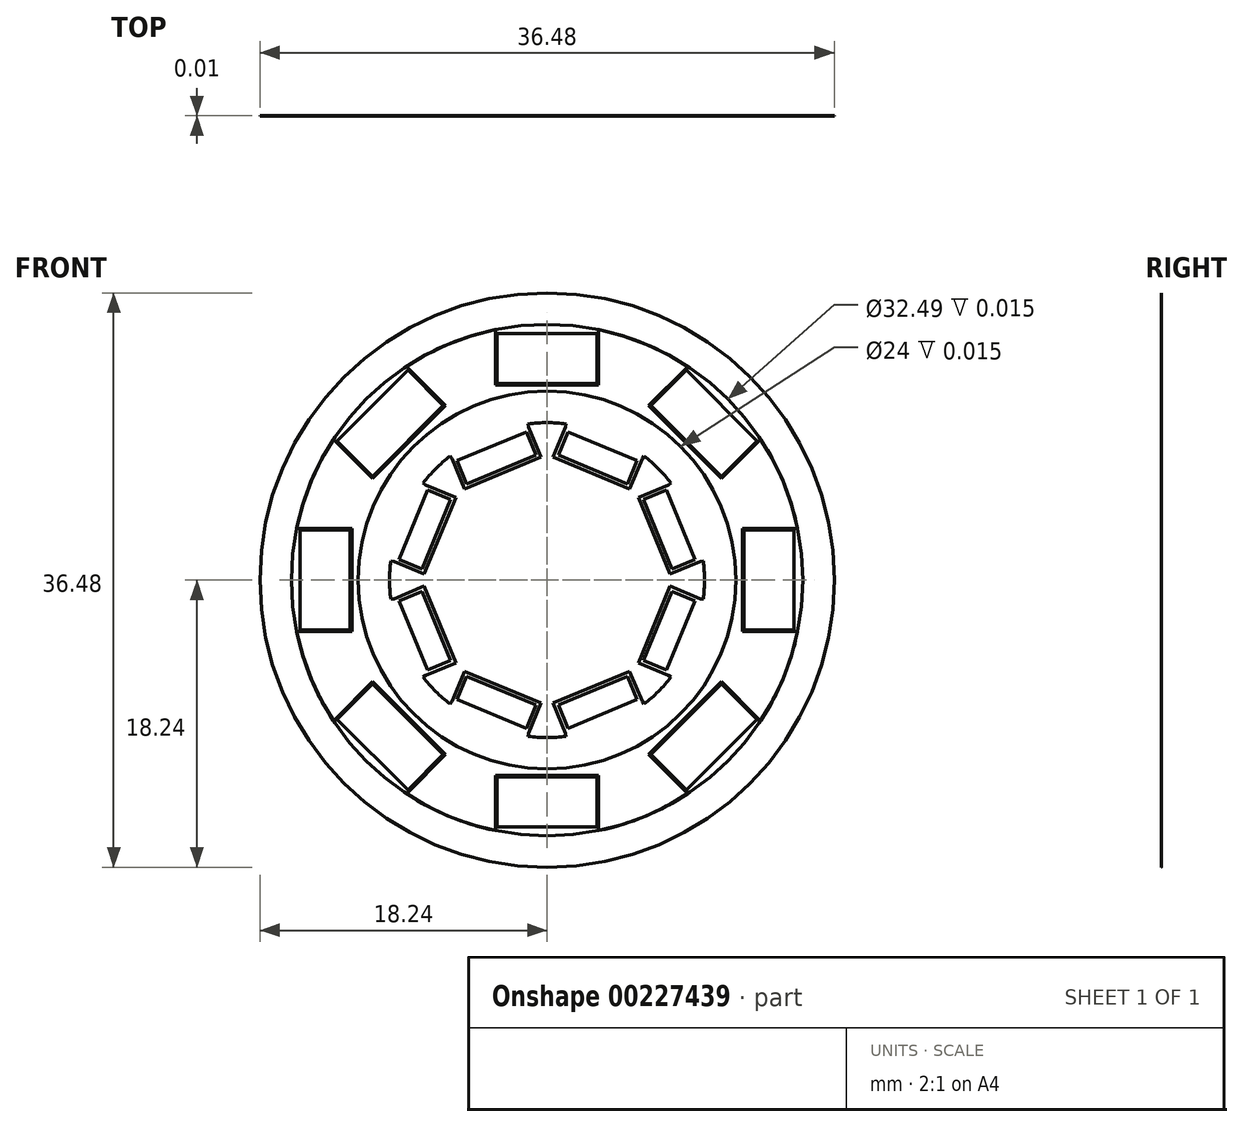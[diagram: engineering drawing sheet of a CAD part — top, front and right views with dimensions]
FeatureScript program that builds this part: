
annotation { "Feature Type Name" : "Feature", "Feature Type Description" : "" }
export const myFeature = defineFeature(function(context is Context, id is Id, definition is map)
    precondition{}
    {
        {
            var Q0;
            Q0=qCreatedBy(makeId("Front.planeOp"),FACE);
            var sketch = newSketch(context, id + "F0", { "sketchPlane" : qUnion([Q0])});
            skLineSegment(sketch, "E0.bottom", {"start": v(-3.17, 12.5) * mm, "end": v(3.17, 12.5) * mm});
            skLineSegment(sketch, "E0.top", {"start": v(-3.17, 15.68) * mm, "end": v(3.17, 15.68) * mm});
            skLineSegment(sketch, "E0.left", {"start": v(-3.18, 12.5) * mm, "end": v(-3.18, 15.68) * mm});
            skLineSegment(sketch, "E0.right", {"start": v(3.17, 12.5) * mm, "end": v(3.17, 15.68) * mm});
            skCircle(sketch, "E1", {"center": v(0, 0) * mm, "radius": 12.5 * mm, "construction": true});
            skCircle(sketch, "E2", {"center": v(0, 0) * mm, "radius": 9.5 * mm, "construction": true});
            skPoint(sketch, "E3.firstSnap0", {"position": v(-3.17, 14.09) * mm});
            skLineSegment(sketch, "E4", {"start": v(0, 0) * mm, "end": v(0, 38.25) * mm, "construction": true});
            skLineSegment(sketch, "E5.bottom", {"start": v(-2.38, 7.6) * mm, "end": v(2.38, 7.6) * mm});
            skLineSegment(sketch, "E5.top", {"start": v(-2.38, 9.2) * mm, "end": v(2.38, 9.2) * mm});
            skLineSegment(sketch, "E5.left", {"start": v(-2.38, 7.6) * mm, "end": v(-2.38, 9.2) * mm});
            skLineSegment(sketch, "E5.right", {"start": v(2.38, 7.6) * mm, "end": v(2.38, 9.2) * mm});
            skCircle(sketch, "E6", {"center": v(0, 0) * mm, "radius": 16 * mm, "construction": true});
            skCircle(sketch, "E7", {"center": v(0, 0) * mm, "radius": 18.24 * mm});
            skCircle(sketch, "E8", {"center": v(0, 0) * mm, "radius": 7.6 * mm, "construction": true});
            skCircle(sketch, "E9", {"center": v(0, 0) * mm, "radius": 5.36 * mm});
            skCircle(sketch, "E10", {"center": v(0, 0) * mm, "radius": 16.24 * mm});
            skCircle(sketch, "E11", {"center": v(0, 0) * mm, "radius": 7.36 * mm});
            skSolve(sketch);
        }
        {
            var Q0;
            Q0=makeQuery(id+"F0.imprint","IMPRINT",FACE,{"disambiguationData":[TD([[makeQuery(id+"F0.imprint","IMPRINT",EDGE,{"derivedFrom":sQuery(id+"F0.wireOp",EDGE,"E7")}),1.0]])]});
            var Q1;
            Q1=makeQuery(id+"F0.imprint","IMPRINT",FACE,{"disambiguationData":[TD([[makeQuery(id+"F0.imprint","IMPRINT",EDGE,{"derivedFrom":sQuery(id+"F0.wireOp",EDGE,"E0.bottom")}),1.0]])]});
            var Q2;
            Q2=makeQuery(id+"F0.imprint","IMPRINT",FACE,{"disambiguationData":[TD([[makeQuery(id+"F0.imprint","IMPRINT",EDGE,{"derivedFrom":sQuery(id+"F0.wireOp",EDGE,"E5.bottom")}),1.0]])]});
            var Q3;
            Q3=makeQuery(id+"F0.imprint","IMPRINT",FACE,{"disambiguationData":[TD([[makeQuery(id+"F0.imprint","IMPRINT",EDGE,{"derivedFrom":sQuery(id+"F0.wireOp",EDGE,"E9")}),-1.0]])]});
            extrude(context, id + "F1", {"entities" : qUnion([Q0, Q1, Q2, Q3]), "depth" : 3 / 203.2 * mm});
        }
        {
            var Q0;
            Q0=qCreatedBy(makeId("Right.planeOp"),FACE);
            var sketch = newSketch(context, id + "F2", { "sketchPlane" : qUnion([Q0])});
            skLineSegment(sketch, "E12", {"start": v(0, 0) * mm, "end": v(120.85, 0) * mm});
            skSolve(sketch);
        }
        {
            var Q0;
            Q0=makeQuery(id+"F1.opExtrude","SWEPT_BODY",BODY,{"disambiguationData":[OSD([sQuery(id+"F0.wireOp",EDGE,"E5.bottom"),sQuery(id+"F0.wireOp",EDGE,"E5.top"),sQuery(id+"F0.wireOp",EDGE,"E5.left"),sQuery(id+"F0.wireOp",EDGE,"E5.right")])]});
            var Q1;
            Q1=makeQuery(id+"F1.opExtrude","SWEPT_BODY",BODY,{"disambiguationData":[OSD([sQuery(id+"F0.wireOp",EDGE,"E0.bottom"),sQuery(id+"F0.wireOp",EDGE,"E0.top"),sQuery(id+"F0.wireOp",EDGE,"E0.left"),sQuery(id+"F0.wireOp",EDGE,"E0.right")])]});
            var Q2;
            Q2=sQuery(id+"F2.wireOp",EDGE,"E12");
            circularPattern(context, id + "F3", {"entities" : qUnion([Q0, Q1]), "axis" : qUnion([Q2]), "angle" : 360 * degree, "instanceCount" : 8, "equalSpace" : true});
        }
        {
            var Q0;
            Q0=qCreatedBy(makeId("Front.planeOp"),FACE);
            var sketch = newSketch(context, id + "F4", { "sketchPlane" : qUnion([Q0])});
            skCircle(sketch, "E13.0", {"center": v(0, 0) * mm, "radius": 7.36 * mm});
            skArc(sketch, "E14", {"start": v(-8.7, 4.91) * mm, "mid": v(-9.24, 3.83) * mm, "end": v(-9.63, 2.68) * mm});
            skLineSegment(sketch, "E15.1", {"start": v(2.63, 7.36) * mm, "end": v(2.63, 9.45) * mm});
            skLineSegment(sketch, "E15.2", {"start": v(-2.63, 7.36) * mm, "end": v(2.63, 7.36) * mm});
            skLineSegment(sketch, "E15.3", {"start": v(-2.63, 9.45) * mm, "end": v(-2.63, 7.36) * mm});
            skLineSegment(sketch, "E16", {"start": v(-2.63, 9.45) * mm, "end": v(-2.68, 9.63) * mm});
            skLineSegment(sketch, "E17", {"start": v(2.63, 9.45) * mm, "end": v(2.68, 9.63) * mm});
            skLineSegment(sketch, "E18.1.0", {"start": v(-3.34, 7.06) * mm, "end": v(-4.82, 8.54) * mm});
            skLineSegment(sketch, "E18.1.1", {"start": v(-8.54, 4.82) * mm, "end": v(-7.06, 3.34) * mm});
            skLineSegment(sketch, "E18.1.2", {"start": v(-7.06, 3.34) * mm, "end": v(-3.34, 7.06) * mm});
            skLineSegment(sketch, "E18.1.3", {"start": v(-4.82, 8.54) * mm, "end": v(-4.91, 8.7) * mm});
            skLineSegment(sketch, "E18.1.4", {"start": v(-8.54, 4.82) * mm, "end": v(-8.7, 4.91) * mm});
            skLineSegment(sketch, "E18.2.0", {"start": v(-7.36, 2.63) * mm, "end": v(-9.45, 2.63) * mm});
            skLineSegment(sketch, "E18.2.1", {"start": v(-9.45, -2.63) * mm, "end": v(-7.36, -2.63) * mm});
            skLineSegment(sketch, "E18.2.2", {"start": v(-7.36, -2.63) * mm, "end": v(-7.36, 2.63) * mm});
            skLineSegment(sketch, "E18.2.3", {"start": v(-9.45, 2.63) * mm, "end": v(-9.63, 2.68) * mm});
            skLineSegment(sketch, "E18.2.4", {"start": v(-9.45, -2.63) * mm, "end": v(-9.63, -2.68) * mm});
            skLineSegment(sketch, "E18.3.0", {"start": v(-7.06, -3.34) * mm, "end": v(-8.54, -4.82) * mm});
            skLineSegment(sketch, "E18.3.1", {"start": v(-4.82, -8.54) * mm, "end": v(-3.34, -7.06) * mm});
            skLineSegment(sketch, "E18.3.2", {"start": v(-3.34, -7.06) * mm, "end": v(-7.06, -3.34) * mm});
            skLineSegment(sketch, "E18.3.3", {"start": v(-8.54, -4.82) * mm, "end": v(-8.7, -4.91) * mm});
            skLineSegment(sketch, "E18.3.4", {"start": v(-4.82, -8.54) * mm, "end": v(-4.91, -8.7) * mm});
            skLineSegment(sketch, "E18.4.0", {"start": v(-2.63, -7.36) * mm, "end": v(-2.63, -9.45) * mm});
            skLineSegment(sketch, "E18.4.1", {"start": v(2.63, -9.45) * mm, "end": v(2.63, -7.36) * mm});
            skLineSegment(sketch, "E18.4.2", {"start": v(2.63, -7.36) * mm, "end": v(-2.63, -7.36) * mm});
            skLineSegment(sketch, "E18.4.3", {"start": v(-2.63, -9.45) * mm, "end": v(-2.68, -9.63) * mm});
            skLineSegment(sketch, "E18.4.4", {"start": v(2.63, -9.45) * mm, "end": v(2.68, -9.63) * mm});
            skLineSegment(sketch, "E18.5.0", {"start": v(3.34, -7.06) * mm, "end": v(4.82, -8.54) * mm});
            skLineSegment(sketch, "E18.5.1", {"start": v(8.54, -4.82) * mm, "end": v(7.06, -3.34) * mm});
            skLineSegment(sketch, "E18.5.2", {"start": v(7.06, -3.34) * mm, "end": v(3.34, -7.06) * mm});
            skLineSegment(sketch, "E18.5.3", {"start": v(4.82, -8.54) * mm, "end": v(4.91, -8.7) * mm});
            skLineSegment(sketch, "E18.5.4", {"start": v(8.54, -4.82) * mm, "end": v(8.7, -4.91) * mm});
            skLineSegment(sketch, "E18.6.0", {"start": v(7.36, -2.63) * mm, "end": v(9.45, -2.63) * mm});
            skLineSegment(sketch, "E18.6.1", {"start": v(9.45, 2.63) * mm, "end": v(7.36, 2.63) * mm});
            skLineSegment(sketch, "E18.6.2", {"start": v(7.36, 2.63) * mm, "end": v(7.36, -2.63) * mm});
            skLineSegment(sketch, "E18.6.3", {"start": v(9.45, -2.63) * mm, "end": v(9.63, -2.68) * mm});
            skLineSegment(sketch, "E18.6.4", {"start": v(9.45, 2.63) * mm, "end": v(9.63, 2.68) * mm});
            skLineSegment(sketch, "E18.7.0", {"start": v(7.06, 3.34) * mm, "end": v(8.54, 4.82) * mm});
            skLineSegment(sketch, "E18.7.1", {"start": v(4.82, 8.54) * mm, "end": v(3.34, 7.06) * mm});
            skLineSegment(sketch, "E18.7.2", {"start": v(3.34, 7.06) * mm, "end": v(7.06, 3.34) * mm});
            skLineSegment(sketch, "E18.7.3", {"start": v(8.54, 4.82) * mm, "end": v(8.7, 4.91) * mm});
            skLineSegment(sketch, "E18.7.4", {"start": v(4.82, 8.54) * mm, "end": v(4.91, 8.7) * mm});
            skArc(sketch, "E19.trimOffspring", {"start": v(-2.68, 9.63) * mm, "mid": v(-3.83, 9.24) * mm, "end": v(-4.91, 8.7) * mm});
            skArc(sketch, "E20.trimOffspring", {"start": v(4.91, 8.7) * mm, "mid": v(3.83, 9.24) * mm, "end": v(2.68, 9.63) * mm});
            skArc(sketch, "E21.trimOffspring", {"start": v(-9.63, -2.68) * mm, "mid": v(-9.24, -3.83) * mm, "end": v(-8.7, -4.91) * mm});
            skArc(sketch, "E22.trimOffspring", {"start": v(-4.91, -8.7) * mm, "mid": v(-3.83, -9.24) * mm, "end": v(-2.68, -9.63) * mm});
            skArc(sketch, "E23.trimOffspring", {"start": v(2.68, -9.63) * mm, "mid": v(3.83, -9.24) * mm, "end": v(4.91, -8.7) * mm});
            skArc(sketch, "E24.trimOffspring", {"start": v(8.7, -4.91) * mm, "mid": v(9.24, -3.83) * mm, "end": v(9.63, -2.68) * mm});
            skArc(sketch, "E25.trimOffspring", {"start": v(9.63, 2.68) * mm, "mid": v(9.24, 3.83) * mm, "end": v(8.7, 4.91) * mm});
            skSolve(sketch);
        }
        {
            var Q0;
            Q0 = qSketchRegion(id + "F4", true);
            extrude(context, id + "F5", {"entities" : qUnion([Q0]), "operationType" : NewBodyOperationType.ADD, "depth" : 3 / 203.2 * mm});
        }
        {
            var Q0;
            Q0=qCreatedBy(makeId("Front.planeOp"),FACE);
            var sketch = newSketch(context, id + "F6", { "sketchPlane" : qUnion([Q0])});
            skCircle(sketch, "E26", {"center": v(0, 0) * mm, "radius": 12 * mm});
            skArc(sketch, "E27.0", {"start": v(-13.58, 8.91) * mm, "mid": v(-15, 6.22) * mm, "end": v(-15.9, 3.3) * mm});
            skLineSegment(sketch, "E28.1", {"start": v(3.27, 12.4) * mm, "end": v(3.27, 15.78) * mm});
            skLineSegment(sketch, "E28.2", {"start": v(-3.28, 12.4) * mm, "end": v(3.27, 12.4) * mm});
            skLineSegment(sketch, "E28.3", {"start": v(-3.28, 15.78) * mm, "end": v(-3.28, 12.4) * mm});
            skLineSegment(sketch, "E29", {"start": v(-3.28, 15.78) * mm, "end": v(-3.3, 15.9) * mm});
            skLineSegment(sketch, "E30", {"start": v(3.27, 15.78) * mm, "end": v(3.3, 15.9) * mm});
            skLineSegment(sketch, "E31.1.0", {"start": v(-13.47, 8.84) * mm, "end": v(-11.08, 6.45) * mm});
            skLineSegment(sketch, "E31.1.1", {"start": v(-11.08, 6.45) * mm, "end": v(-6.45, 11.08) * mm});
            skLineSegment(sketch, "E31.1.2", {"start": v(-6.45, 11.08) * mm, "end": v(-8.84, 13.47) * mm});
            skLineSegment(sketch, "E31.1.3", {"start": v(-13.47, 8.84) * mm, "end": v(-13.58, 8.91) * mm});
            skLineSegment(sketch, "E31.1.4", {"start": v(-8.84, 13.47) * mm, "end": v(-8.91, 13.58) * mm});
            skLineSegment(sketch, "E31.2.0", {"start": v(-15.78, -3.28) * mm, "end": v(-12.4, -3.28) * mm});
            skLineSegment(sketch, "E31.2.1", {"start": v(-12.4, -3.28) * mm, "end": v(-12.4, 3.27) * mm});
            skLineSegment(sketch, "E31.2.2", {"start": v(-12.4, 3.27) * mm, "end": v(-15.78, 3.27) * mm});
            skLineSegment(sketch, "E31.2.3", {"start": v(-15.78, -3.28) * mm, "end": v(-15.9, -3.3) * mm});
            skLineSegment(sketch, "E31.2.4", {"start": v(-15.78, 3.27) * mm, "end": v(-15.9, 3.3) * mm});
            skLineSegment(sketch, "E31.3.0", {"start": v(-8.84, -13.47) * mm, "end": v(-6.45, -11.08) * mm});
            skLineSegment(sketch, "E31.3.1", {"start": v(-6.45, -11.08) * mm, "end": v(-11.08, -6.45) * mm});
            skLineSegment(sketch, "E31.3.2", {"start": v(-11.08, -6.45) * mm, "end": v(-13.47, -8.84) * mm});
            skLineSegment(sketch, "E31.3.3", {"start": v(-8.84, -13.47) * mm, "end": v(-8.91, -13.58) * mm});
            skLineSegment(sketch, "E31.3.4", {"start": v(-13.47, -8.84) * mm, "end": v(-13.58, -8.91) * mm});
            skLineSegment(sketch, "E31.4.0", {"start": v(3.28, -15.78) * mm, "end": v(3.28, -12.4) * mm});
            skLineSegment(sketch, "E31.4.1", {"start": v(3.28, -12.4) * mm, "end": v(-3.27, -12.4) * mm});
            skLineSegment(sketch, "E31.4.2", {"start": v(-3.27, -12.4) * mm, "end": v(-3.27, -15.78) * mm});
            skLineSegment(sketch, "E31.4.3", {"start": v(3.28, -15.78) * mm, "end": v(3.3, -15.9) * mm});
            skLineSegment(sketch, "E31.4.4", {"start": v(-3.28, -15.78) * mm, "end": v(-3.3, -15.9) * mm});
            skLineSegment(sketch, "E31.5.0", {"start": v(13.47, -8.84) * mm, "end": v(11.08, -6.45) * mm});
            skLineSegment(sketch, "E31.5.1", {"start": v(11.08, -6.45) * mm, "end": v(6.45, -11.08) * mm});
            skLineSegment(sketch, "E31.5.2", {"start": v(6.45, -11.08) * mm, "end": v(8.84, -13.47) * mm});
            skLineSegment(sketch, "E31.5.3", {"start": v(13.47, -8.84) * mm, "end": v(13.58, -8.91) * mm});
            skLineSegment(sketch, "E31.5.4", {"start": v(8.84, -13.47) * mm, "end": v(8.91, -13.58) * mm});
            skLineSegment(sketch, "E31.6.0", {"start": v(15.78, 3.28) * mm, "end": v(12.4, 3.28) * mm});
            skLineSegment(sketch, "E31.6.1", {"start": v(12.4, 3.28) * mm, "end": v(12.4, -3.27) * mm});
            skLineSegment(sketch, "E31.6.2", {"start": v(12.4, -3.27) * mm, "end": v(15.78, -3.27) * mm});
            skLineSegment(sketch, "E31.6.3", {"start": v(15.78, 3.28) * mm, "end": v(15.9, 3.3) * mm});
            skLineSegment(sketch, "E31.6.4", {"start": v(15.78, -3.28) * mm, "end": v(15.9, -3.3) * mm});
            skLineSegment(sketch, "E31.7.0", {"start": v(8.84, 13.47) * mm, "end": v(6.45, 11.08) * mm});
            skLineSegment(sketch, "E31.7.1", {"start": v(6.45, 11.08) * mm, "end": v(11.08, 6.45) * mm});
            skLineSegment(sketch, "E31.7.2", {"start": v(11.08, 6.45) * mm, "end": v(13.47, 8.84) * mm});
            skLineSegment(sketch, "E31.7.3", {"start": v(8.84, 13.47) * mm, "end": v(8.91, 13.58) * mm});
            skLineSegment(sketch, "E31.7.4", {"start": v(13.47, 8.84) * mm, "end": v(13.58, 8.91) * mm});
            skArc(sketch, "E32.trimOffspring", {"start": v(-3.3, 15.9) * mm, "mid": v(-6.22, 15) * mm, "end": v(-8.91, 13.58) * mm});
            skArc(sketch, "E33.trimOffspring", {"start": v(8.91, 13.58) * mm, "mid": v(6.22, 15) * mm, "end": v(3.3, 15.9) * mm});
            skArc(sketch, "E34.trimOffspring", {"start": v(15.9, 3.3) * mm, "mid": v(15, 6.22) * mm, "end": v(13.58, 8.91) * mm});
            skArc(sketch, "E35.trimOffspring", {"start": v(13.58, -8.91) * mm, "mid": v(15, -6.22) * mm, "end": v(15.9, -3.3) * mm});
            skArc(sketch, "E36.trimOffspring", {"start": v(3.3, -15.9) * mm, "mid": v(6.22, -15) * mm, "end": v(8.91, -13.58) * mm});
            skArc(sketch, "E37.trimOffspring", {"start": v(-8.91, -13.58) * mm, "mid": v(-6.22, -15) * mm, "end": v(-3.3, -15.9) * mm});
            skArc(sketch, "E38.trimOffspring", {"start": v(-15.9, -3.3) * mm, "mid": v(-15, -6.22) * mm, "end": v(-13.58, -8.91) * mm});
            skSolve(sketch);
        }
        {
            var Q0;
            Q0 = qSketchRegion(id + "F6", true);
            extrude(context, id + "F7", {"entities" : qUnion([Q0]), "depth" : 3 / 203.2 * mm});
        }
        {
            var Q0;
            Q0=makeQuery(id+"F3.opPattern","COPY",BODY,{"derivedFrom":makeQuery(id+"F1.opExtrude","SWEPT_BODY",BODY,{"disambiguationData":[OSD([sQuery(id+"F0.wireOp",EDGE,"E5.bottom"),sQuery(id+"F0.wireOp",EDGE,"E5.top"),sQuery(id+"F0.wireOp",EDGE,"E5.left"),sQuery(id+"F0.wireOp",EDGE,"E5.right")])]}),"instanceName":"7"});
            var Q1;
            Q1=makeQuery(id+"F1.opExtrude","SWEPT_BODY",BODY,{"disambiguationData":[OSD([sQuery(id+"F0.wireOp",EDGE,"E5.bottom"),sQuery(id+"F0.wireOp",EDGE,"E5.top"),sQuery(id+"F0.wireOp",EDGE,"E5.left"),sQuery(id+"F0.wireOp",EDGE,"E5.right")])]});
            var Q2;
            Q2=makeQuery(id+"F3.opPattern","COPY",BODY,{"derivedFrom":makeQuery(id+"F1.opExtrude","SWEPT_BODY",BODY,{"disambiguationData":[OSD([sQuery(id+"F0.wireOp",EDGE,"E5.bottom"),sQuery(id+"F0.wireOp",EDGE,"E5.top"),sQuery(id+"F0.wireOp",EDGE,"E5.left"),sQuery(id+"F0.wireOp",EDGE,"E5.right")])]}),"instanceName":"1"});
            var Q3;
            Q3=makeQuery(id+"F3.opPattern","COPY",BODY,{"derivedFrom":makeQuery(id+"F1.opExtrude","SWEPT_BODY",BODY,{"disambiguationData":[OSD([sQuery(id+"F0.wireOp",EDGE,"E5.bottom"),sQuery(id+"F0.wireOp",EDGE,"E5.top"),sQuery(id+"F0.wireOp",EDGE,"E5.left"),sQuery(id+"F0.wireOp",EDGE,"E5.right")])]}),"instanceName":"2"});
            var Q4;
            Q4=makeQuery(id+"F3.opPattern","COPY",BODY,{"derivedFrom":makeQuery(id+"F1.opExtrude","SWEPT_BODY",BODY,{"disambiguationData":[OSD([sQuery(id+"F0.wireOp",EDGE,"E5.bottom"),sQuery(id+"F0.wireOp",EDGE,"E5.top"),sQuery(id+"F0.wireOp",EDGE,"E5.left"),sQuery(id+"F0.wireOp",EDGE,"E5.right")])]}),"instanceName":"3"});
            var Q5;
            Q5=makeQuery(id+"F3.opPattern","COPY",BODY,{"derivedFrom":makeQuery(id+"F1.opExtrude","SWEPT_BODY",BODY,{"disambiguationData":[OSD([sQuery(id+"F0.wireOp",EDGE,"E5.bottom"),sQuery(id+"F0.wireOp",EDGE,"E5.top"),sQuery(id+"F0.wireOp",EDGE,"E5.left"),sQuery(id+"F0.wireOp",EDGE,"E5.right")])]}),"instanceName":"4"});
            var Q6;
            Q6=makeQuery(id+"F3.opPattern","COPY",BODY,{"derivedFrom":makeQuery(id+"F1.opExtrude","SWEPT_BODY",BODY,{"disambiguationData":[OSD([sQuery(id+"F0.wireOp",EDGE,"E5.bottom"),sQuery(id+"F0.wireOp",EDGE,"E5.top"),sQuery(id+"F0.wireOp",EDGE,"E5.left"),sQuery(id+"F0.wireOp",EDGE,"E5.right")])]}),"instanceName":"5"});
            var Q7;
            Q7=makeQuery(id+"F3.opPattern","COPY",BODY,{"derivedFrom":makeQuery(id+"F1.opExtrude","SWEPT_BODY",BODY,{"disambiguationData":[OSD([sQuery(id+"F0.wireOp",EDGE,"E5.bottom"),sQuery(id+"F0.wireOp",EDGE,"E5.top"),sQuery(id+"F0.wireOp",EDGE,"E5.left"),sQuery(id+"F0.wireOp",EDGE,"E5.right")])]}),"instanceName":"6"});
            var Q8;
            Q8=makeQuery(id+"F1.opExtrude","SWEPT_BODY",BODY,{"disambiguationData":[OSD([sQuery(id+"F0.wireOp",EDGE,"E9"),sQuery(id+"F0.wireOp",EDGE,"E11")])]});
            var Q9;
            Q9=sQuery(id+"F2.wireOp",EDGE,"E12");
            var Q10;
            Q10=sQuery(id+"F2.wireOp",EDGE,"E12");
            transform(context, id + "F8", {"entities" : qUnion([Q0, Q1, Q2, Q3, Q4, Q5, Q6, Q7, Q8]), "transformType" : TransformType.ROTATION, "transformAxis" : qUnion([Q10]), "angle" : 22.5 * degree, "makeCopy" : false});
        }
    });
